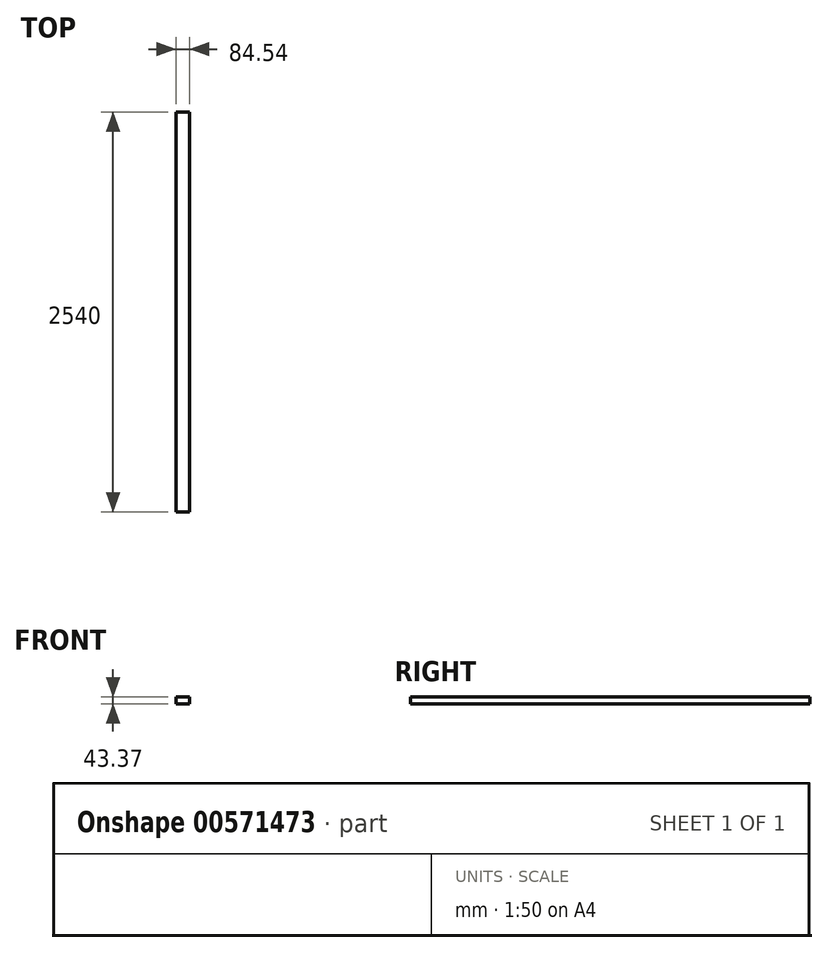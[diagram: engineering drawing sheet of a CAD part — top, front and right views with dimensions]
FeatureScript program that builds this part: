
annotation { "Feature Type Name" : "Feature", "Feature Type Description" : "" }
export const myFeature = defineFeature(function(context is Context, id is Id, definition is map)
    precondition{}
    {
        {
            var Q0;
            Q0=qCreatedBy(makeId("Front.planeOp"),FACE);
            var sketch = newSketch(context, id + "F0", { "sketchPlane" : qUnion([Q0])});
            skLineSegment(sketch, "E0.bottom", {"start": v(-40.82, 17.24) * mm, "end": v(43.72, 17.24) * mm});
            skLineSegment(sketch, "E0.top", {"start": v(-40.82, -26.13) * mm, "end": v(43.72, -26.13) * mm});
            skLineSegment(sketch, "E0.left", {"start": v(-40.82, 17.24) * mm, "end": v(-40.82, -26.13) * mm});
            skLineSegment(sketch, "E0.right", {"start": v(43.72, 17.24) * mm, "end": v(43.72, -26.13) * mm});
            skSolve(sketch);
        }
        {
            var Q0;
            Q0=makeQuery(id+"F0.imprint","IMPRINT",FACE,{"disambiguationData":[TD([[makeQuery(id+"F0.imprint","IMPRINT",EDGE,{"derivedFrom":sQuery(id+"F0.wireOp",EDGE,"E0.bottom")}),-1.0]])]});
            extrude(context, id + "F1", {"entities" : qUnion([Q0]), "depth" : 2540 * mm, "offsetDistance" : 25.4 * mm});
        }
    });
